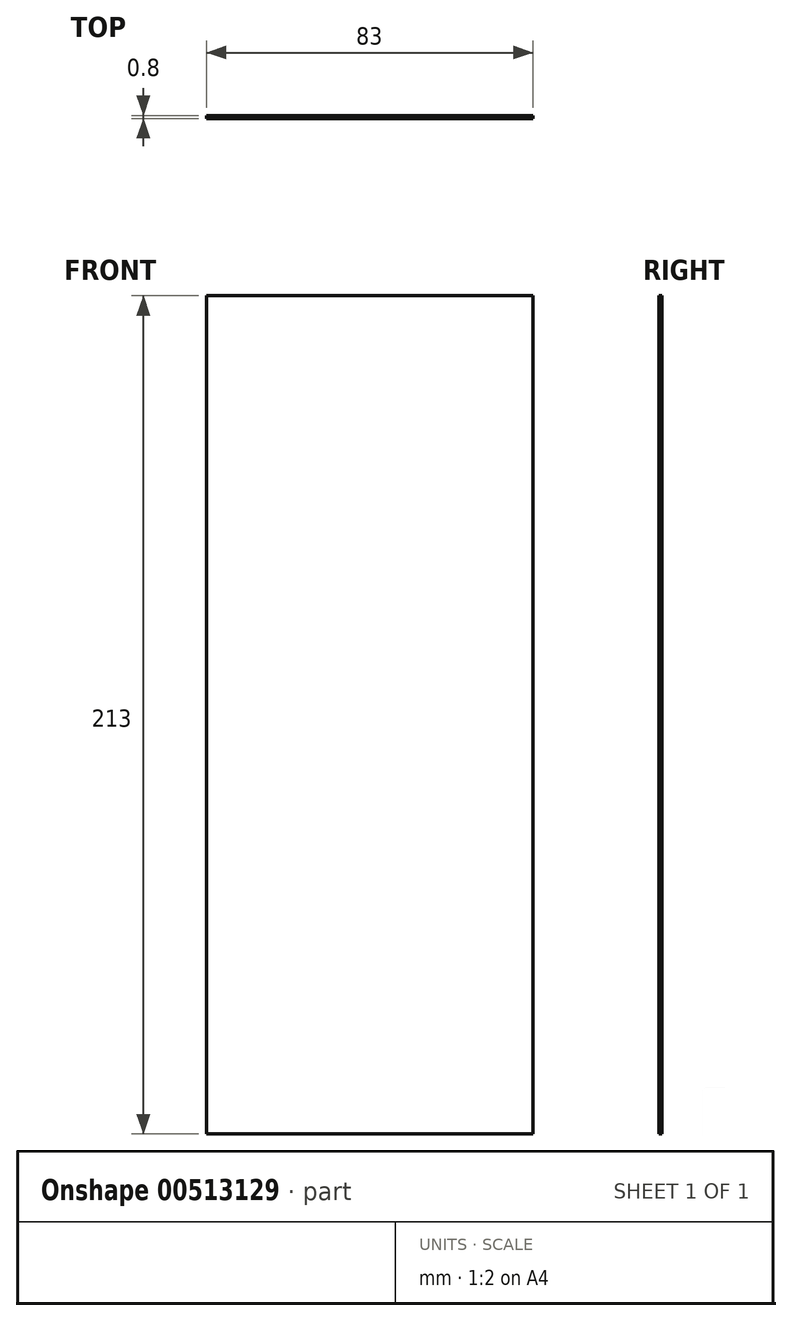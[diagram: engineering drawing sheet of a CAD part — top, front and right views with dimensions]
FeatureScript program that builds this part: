
annotation { "Feature Type Name" : "Feature", "Feature Type Description" : "" }
export const myFeature = defineFeature(function(context is Context, id is Id, definition is map)
    precondition{}
    {
        {
            var Q0;
            Q0=qCreatedBy(makeId("Front.planeOp"),FACE);
            var sketch = newSketch(context, id + "F0", { "sketchPlane" : qUnion([Q0])});
            skLineSegment(sketch, "E0.bottom", {"start": v(-83, 148.67) * mm, "end": v(0, 148.67) * mm});
            skLineSegment(sketch, "E0.top", {"start": v(-83, -64.33) * mm, "end": v(0, -64.33) * mm});
            skLineSegment(sketch, "E0.left", {"start": v(-83, 148.67) * mm, "end": v(-83, -64.33) * mm});
            skLineSegment(sketch, "E0.right", {"start": v(0, 148.67) * mm, "end": v(0, -64.33) * mm});
            skSolve(sketch);
        }
        {
            var Q0;
            Q0=makeQuery(id+"F0.imprint","IMPRINT",FACE,{"disambiguationData":[TD([[makeQuery(id+"F0.imprint","IMPRINT",EDGE,{"derivedFrom":sQuery(id+"F0.wireOp",EDGE,"E0.bottom")}),-1.0]])]});
            extrude(context, id + "F1", {"entities" : qUnion([Q0]), "depth" : 0.8 * mm});
        }
    });
